# Revit family: Faucet-Spray_Kit-KOHLER-Cuff-K-98100IN-1
name_source: partatom
category: Plumbing Fixtures
units: mm (PartAtom-declared; Revit-internal decimal feet)

## family parameters
Cut with Voids When Loaded = No
Host = Face
Maintain Annotation Orientation = No
OmniClass Number = 23.31.11.00
OmniClass Title = Faucets
Part Type = Normal
Room Calculation Point = No
Round Connector Dimension = Use Diameter
Shared = No

## types (6) — shared parameters
ADA Compliant = No
Assembly Code = D2010
CW Connection = Yes
Cold Water Inlet = Cold Water Inlet
Date Modified = 09/05/2024
Default Elevation = 36"
Description = Single-Function Health Faucet, 11.5 lpm
Drain Included = No
Flow Rate = 3 GPM
HW Connection = No
Height = 7 1/2"
Hot Water Inlet = Hot Water Inlet
Length = 2 1/8"
Manufacturer = Kohler Co.
Master Format 2014 = 22 41 39
Master Format 2014 Name = Residential Faucets, Supplies, and Trim
Material = Plastic
Pressure = 72.52 psi
Product Name = Cuff
URL = https://www.kohler.co.in
Vent Connection = No
Waste Connection = No
Waste Water Outlet = Waste Water Outlet
WaterSense Certified = No
Width = 1 3/8"

## per-type parameters (varying)
| type | Finish | Model | Product Page URL | Type |
| CP-Polished Chrome | Kohler-Plastic-CP-Polished_Chrome | K-98100IN-CP | https://www.kohler.co.in | 1 |
| 0-White | Kohler-Plastic-0-White | K-98100IN-0 | https://www.kohler.co.in | 2 |
| 2BL-Black | Kohler-Plastic-2BL-Black | K-98100IN-2BL |  | 3 |
| BL-Matte Black | Kohler-Plastic-BL-Matte_Black | K-98100IN-BL |  | 4 |
| HP1-Peacock | Kohler-Plastic-HP1-Peacock | K-98100IN-HP1 |  | 5 |
| HT1-Honed Truffle | Kohler-Plastic-HT1-Honed_Truffle | K-98100IN-HT1 |  | 6 |

## geometry (parser evidence)
native form markers: Sweep x6
no freeform markers — native parametric forms only
